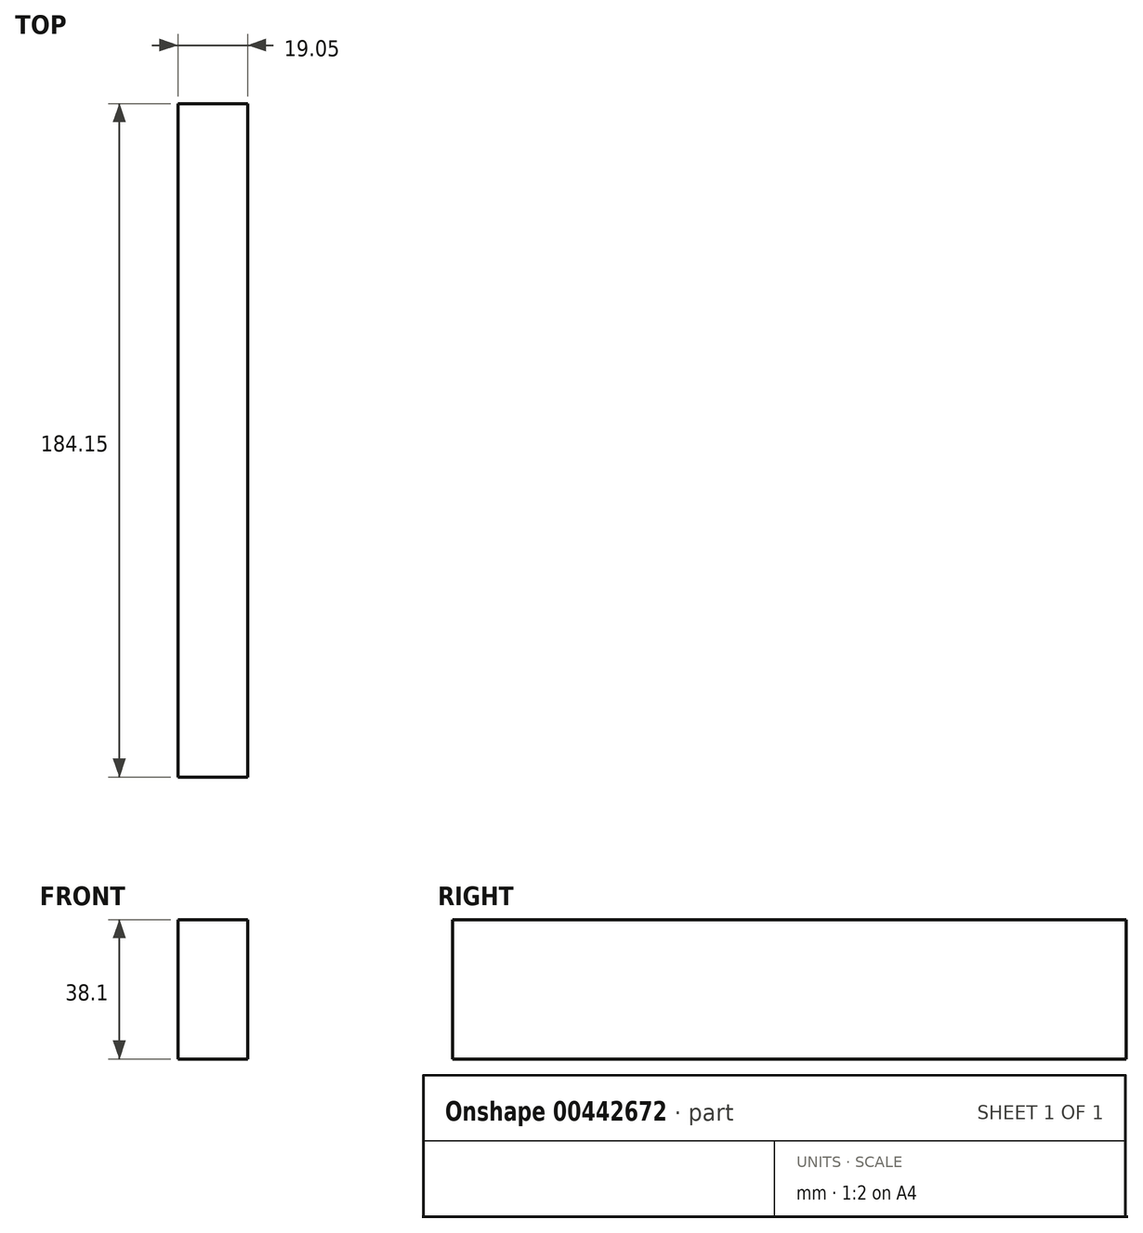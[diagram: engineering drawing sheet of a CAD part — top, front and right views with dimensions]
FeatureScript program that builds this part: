
annotation { "Feature Type Name" : "Feature", "Feature Type Description" : "" }
export const myFeature = defineFeature(function(context is Context, id is Id, definition is map)
    precondition{}
    {
        {
            var Q0;
            Q0=qCreatedBy(makeId("Right.planeOp"),FACE);
            var sketch = newSketch(context, id + "F0", { "sketchPlane" : qUnion([Q0])});
            skLineSegment(sketch, "E0.bottom", {"start": v(0, 0) * mm, "end": v(-184.15, 0) * mm});
            skLineSegment(sketch, "E0.top", {"start": v(0, 38.1) * mm, "end": v(-184.15, 38.1) * mm});
            skLineSegment(sketch, "E0.left", {"start": v(0, 0) * mm, "end": v(0, 38.1) * mm});
            skLineSegment(sketch, "E0.right", {"start": v(-184.15, 0) * mm, "end": v(-184.15, 38.1) * mm});
            skSolve(sketch);
        }
        {
            var Q0;
            Q0 = qSketchRegion(id + "F0", true);
            extrude(context, id + "F1", {"entities" : qUnion([Q0]), "depth" : 19.05 * mm});
        }
    });
